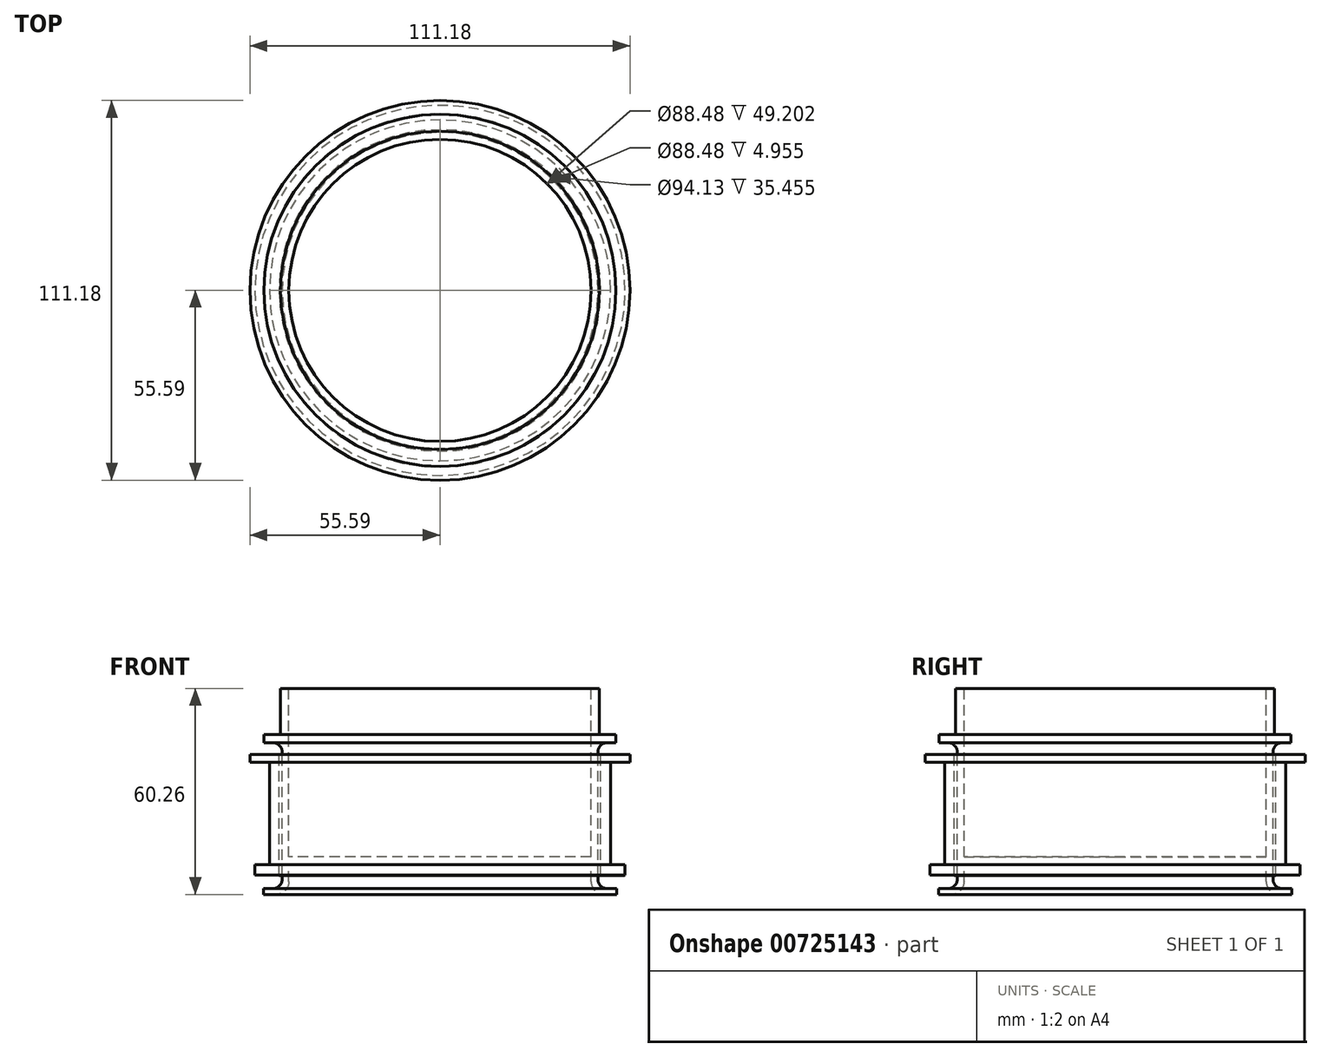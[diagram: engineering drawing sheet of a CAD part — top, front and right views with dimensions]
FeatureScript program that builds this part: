
annotation { "Feature Type Name" : "Feature", "Feature Type Description" : "" }
export const myFeature = defineFeature(function(context is Context, id is Id, definition is map)
    precondition{}
    {
        {
            var Q0;
            Q0=qCreatedBy(makeId("Front.planeOp"),FACE);
            var sketch = newSketch(context, id + "F0", { "sketchPlane" : qUnion([Q0])});
            skLineSegment(sketch, "E0", {"start": v(0, 0) * mm, "end": v(44.24, 0) * mm});
            skLineSegment(sketch, "E1", {"start": v(44.24, 0) * mm, "end": v(44.24, -4.95) * mm});
            skLineSegment(sketch, "E2", {"start": v(48.05, -8.76) * mm, "end": v(51.73, -8.76) * mm});
            skLineSegment(sketch, "E3", {"start": v(51.73, -8.76) * mm, "end": v(51.73, -7) * mm});
            skLineSegment(sketch, "E4", {"start": v(51.73, -7) * mm, "end": v(48.77, -7) * mm});
            skLineSegment(sketch, "E5", {"start": v(46.23, -4.45) * mm, "end": v(46.23, 33.07) * mm});
            skLineSegment(sketch, "E6", {"start": v(48.77, 35.61) * mm, "end": v(51.52, 35.61) * mm});
            skLineSegment(sketch, "E7", {"start": v(51.52, 35.61) * mm, "end": v(51.52, 38.08) * mm});
            skLineSegment(sketch, "E8", {"start": v(51.52, 38.08) * mm, "end": v(46.65, 38.08) * mm});
            skLineSegment(sketch, "E9", {"start": v(46.65, 38.08) * mm, "end": v(46.65, 51.5) * mm});
            skLineSegment(sketch, "E10", {"start": v(46.65, 51.5) * mm, "end": v(44.24, 51.5) * mm});
            skLineSegment(sketch, "E11", {"start": v(44.24, 51.5) * mm, "end": v(44.24, 2.3) * mm});
            skLineSegment(sketch, "E12", {"start": v(44.24, 2.3) * mm, "end": v(0, 2.3) * mm});
            skLineSegment(sketch, "E13", {"start": v(0, 2.3) * mm, "end": v(0, 0) * mm});
            skPoint(sketch, "E14.visualSharp", {"position": v(46.23, -7) * mm});
            skArc(sketch, "E14.filletArc", {"start": v(46.23, -4.45) * mm, "mid": v(46.98, -6.25) * mm, "end": v(48.77, -7) * mm});
            skPoint(sketch, "E15.visualSharp", {"position": v(44.24, -8.76) * mm});
            skArc(sketch, "E15.filletArc", {"start": v(44.24, -4.95) * mm, "mid": v(45.35, -7.65) * mm, "end": v(48.05, -8.76) * mm});
            skPoint(sketch, "E16.visualSharp", {"position": v(46.23, 35.61) * mm});
            skArc(sketch, "E16.filletArc", {"start": v(48.77, 35.61) * mm, "mid": v(46.98, 34.87) * mm, "end": v(46.23, 33.07) * mm});
            skLineSegment(sketch, "E17", {"start": v(47.06, -3.25) * mm, "end": v(47.06, 32.2) * mm});
            skLineSegment(sketch, "E18", {"start": v(47.06, 32.2) * mm, "end": v(55.6, 32.2) * mm});
            skLineSegment(sketch, "E19", {"start": v(55.6, 32.2) * mm, "end": v(55.6, 29.93) * mm});
            skLineSegment(sketch, "E20", {"start": v(55.6, 29.93) * mm, "end": v(49.9, 29.93) * mm});
            skLineSegment(sketch, "E21", {"start": v(49.9, 29.93) * mm, "end": v(49.9, 0) * mm});
            skLineSegment(sketch, "E22", {"start": v(49.9, 0) * mm, "end": v(54.17, 0) * mm});
            skLineSegment(sketch, "E23", {"start": v(54.17, 0) * mm, "end": v(54.17, -3.16) * mm});
            skLineSegment(sketch, "E24", {"start": v(54.17, -3.16) * mm, "end": v(47.06, -3.25) * mm});
            skSolve(sketch);
        }
        {
            var Q0;
            Q0 = qSketchRegion(id + "F0", true);
            var Q1;
            Q1=sQuery(id+"F0.wireOp",EDGE,"E13");
            revolve(context, id + "F1", {"surfaceOperationType" : NewSurfaceOperationType.NEW, "entities" : qUnion([Q0]), "axis" : qUnion([Q1]), "revolveType" : RevolveType.FULL});
        }
    });
